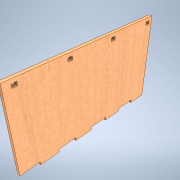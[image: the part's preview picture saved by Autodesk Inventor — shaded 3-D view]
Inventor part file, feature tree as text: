
AUTODESK INVENTOR PART (.ipt)
format: ipt  version: 2021 (Build 250183000, 183)  size: 269,824 bytes
history: native  units: mm
features: extrude x3, sketch x2
ambient origin geometry x8: Origin, YZ Plane, XZ Plane, XY Plane, X Axis, Y Axis, Z Axis, Center Point
bodies: Solid1 (feature_tree)
feature tree (5):
  extrude  "Extrusion1"  Depth=3.0mm TaperAngle=0.0deg
  extrude  "Extrusion5"  Depth=4.0mm
  extrude  "Extrusion6"  Depth=10.0mm TaperAngle=0.0deg
  sketch  "Sketch5"  dims[d1=140.0mm d2=3.0mm d3=0.0mm]
  sketch  "Sketch6"  dims[d67=3.0mm d68=4.0mm d76=10.0mm d77=0.0mm d93=3.1mm d95=3.0mm d96=0.0mm d97=6.0mm d98=50.0mm d100=31.75mm d101=20.0mm d103=38.0mm d106=20.0mm d108=6.1mm d109=10.0mm d111=10.0mm d113=3.0mm d26=0.5mm d27=0.872665mm d28=0.5mm d29=0.872665mm d94=0.5mm]
